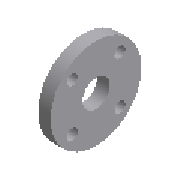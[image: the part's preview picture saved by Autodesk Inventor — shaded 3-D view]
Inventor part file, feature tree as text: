
AUTODESK INVENTOR PART (.ipt)
format: ipt  version: 2023.2 (Build 272271030, 271C)  size: 167,936 bytes
history: native  units: mm (DEFAULTED — no unit token found)
features: other x5, sketch x2, revolve x1, extrude x1, pattern_circular x1
ambient origin geometry x8: Origin, YZ Plane, XZ Plane, XY Plane, X Axis, Y Axis, Z Axis, Center Point
bodies: Solid1 (feature_tree)
feature tree (10):
  sketch  "Sketch1"  dims[d11=90.0deg d0=200.0mm]
  revolve  "Revolution1"  [1 undecoded]
  extrude  "Extrusion1"  Depth=80.0mm
  pattern_circular  "Circular Pattern1"  [2 undecoded]
  other  "Work Axis1"
  other  "Work Point1"
  other  "Work Point2"
  other  "Work Axis2"
  other  "Work Point3"
  sketch  "Sketch2"  dims[d1=20.0mm d2=160.0mm d19=25.4mm d3=0.0mm d4=80.0mm d5=360.0deg d6=90.5mm d7=18.0mm d8=22.5deg]
note: 3 required parameter values undecoded (feature->parameter linkage not recoverable at this tier; creation-order binding heuristic only, values carry confidence <= 0.55)